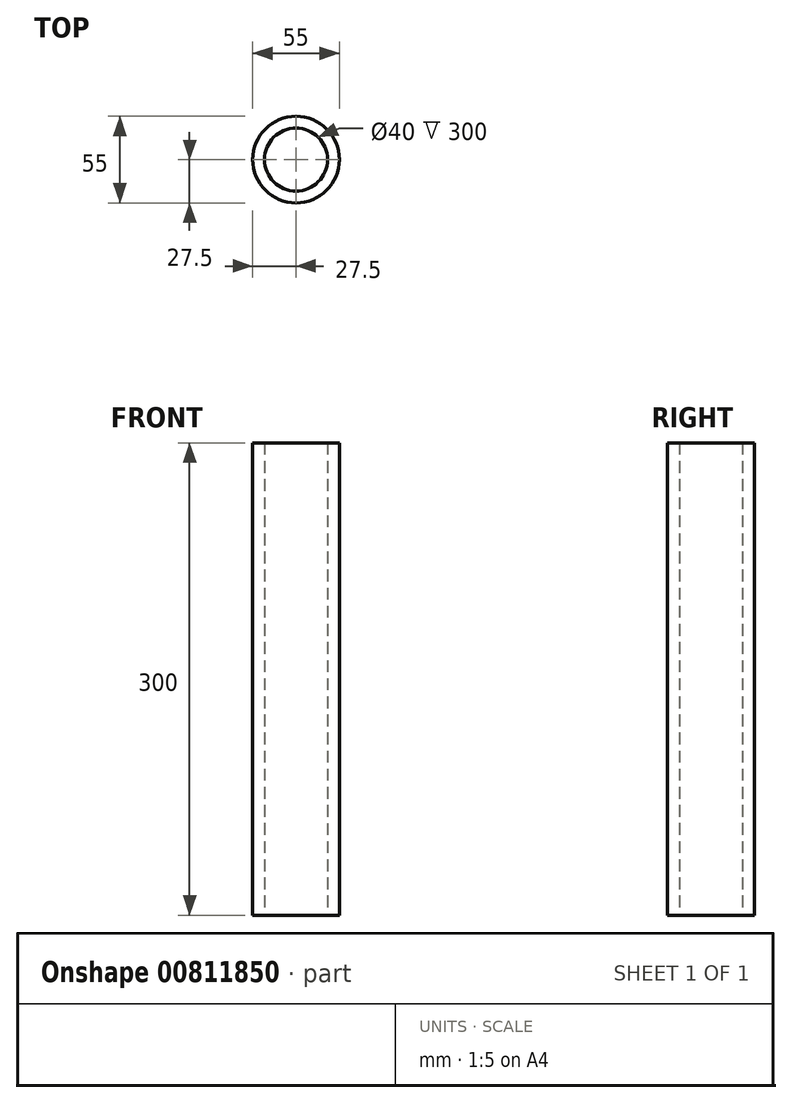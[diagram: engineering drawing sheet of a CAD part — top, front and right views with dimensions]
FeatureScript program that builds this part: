
annotation { "Feature Type Name" : "Feature", "Feature Type Description" : "" }
export const myFeature = defineFeature(function(context is Context, id is Id, definition is map)
    precondition{}
    {
        {
            var Q0;
            Q0=qCreatedBy(makeId("Top.planeOp"),FACE);
            var sketch = newSketch(context, id + "F0", { "sketchPlane" : qUnion([Q0])});
            skCircle(sketch, "E0", {"center": v(0, 0) * mm, "radius": 20 * mm});
            skCircle(sketch, "E1", {"center": v(0, 0) * mm, "radius": 27.5 * mm});
            skSolve(sketch);
        }
        {
            var Q0;
            Q0=makeQuery(id+"F0.imprint","IMPRINT",FACE,{"disambiguationData":[TD([[makeQuery(id+"F0.imprint","IMPRINT",EDGE,{"derivedFrom":sQuery(id+"F0.wireOp",EDGE,"E0")}),-1.0]])]});
            extrude(context, id + "F1", {"entities" : qUnion([Q0]), "depth" : 300 * mm, "offsetDistance" : 25 * mm});
        }
    });
